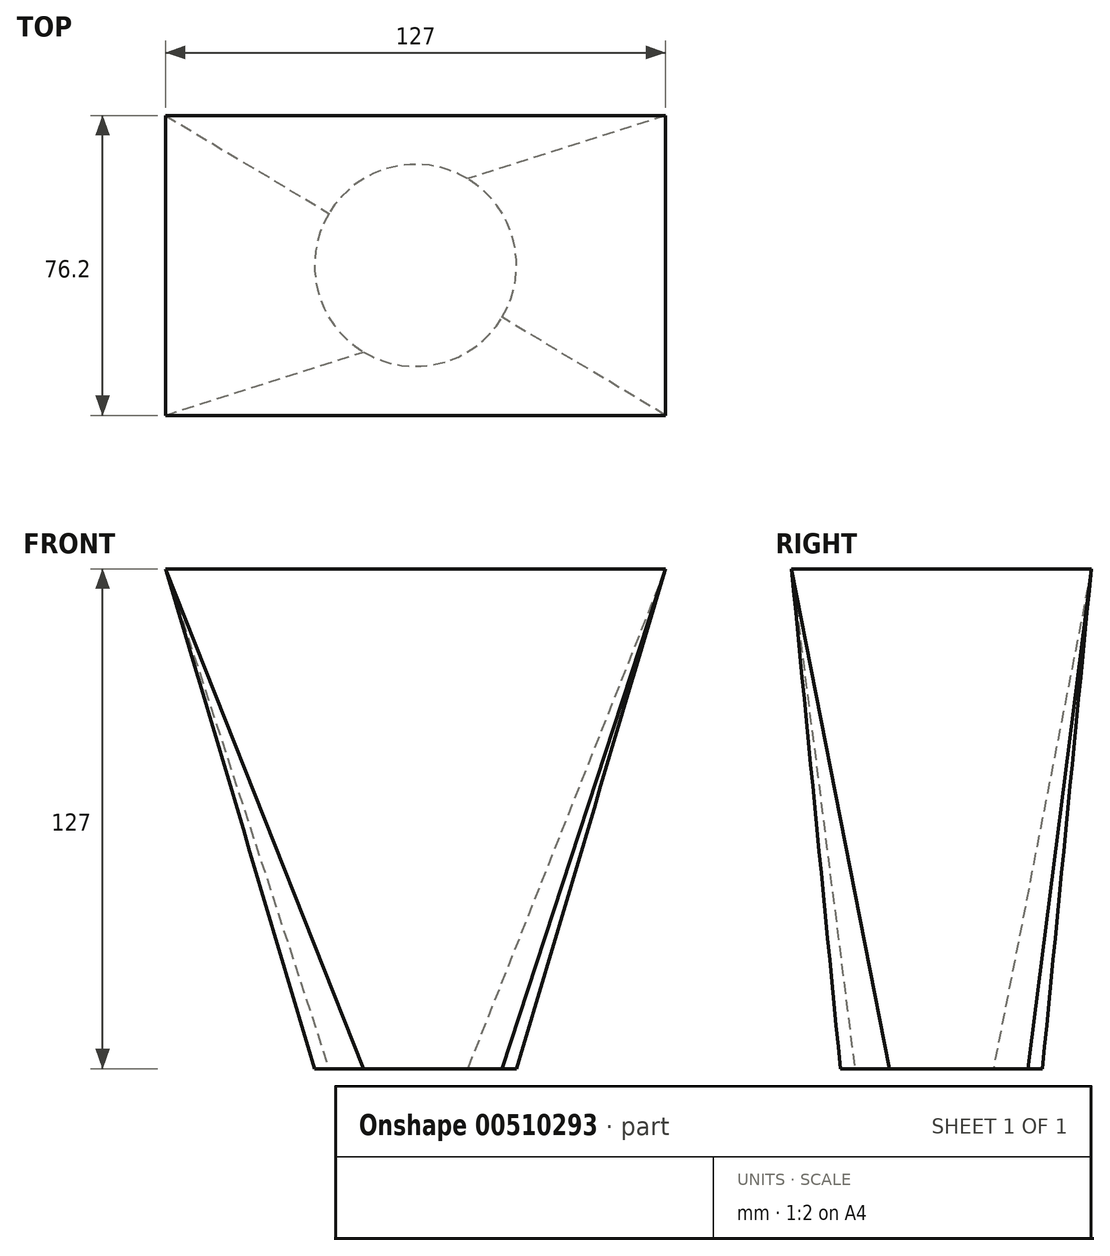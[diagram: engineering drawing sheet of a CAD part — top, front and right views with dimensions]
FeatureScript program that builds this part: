
annotation { "Feature Type Name" : "Feature", "Feature Type Description" : "" }
export const myFeature = defineFeature(function(context is Context, id is Id, definition is map)
    precondition{}
    {
        {
            var Q0;
            Q0=qCreatedBy(makeId("Top.planeOp"),FACE);
            var sketch = newSketch(context, id + "F0", { "sketchPlane" : qUnion([Q0])});
            skCircle(sketch, "E0", {"center": v(0, 0) * mm, "radius": 25.65 * mm});
            skSolve(sketch);
        }
        {
            var Q0;
            Q0=qCreatedBy(makeId("Top.planeOp"),FACE);
            cPlane(context, id + "F1", {"entities" : qUnion([Q0]), "cplaneType" : CPlaneType.OFFSET, "offset" : 127 * mm, "width" : 152.4 * mm, "height" : 152.4 * mm});
        }
        {
            var Q0;
            Q0=qCreatedBy(id+"F1.planeOp",FACE);
            var sketch = newSketch(context, id + "F2", { "sketchPlane" : qUnion([Q0])});
            skLineSegment(sketch, "E1.bottom", {"start": v(63.5, -38.1) * mm, "end": v(-63.5, -38.1) * mm});
            skLineSegment(sketch, "E1.top", {"start": v(63.5, 38.1) * mm, "end": v(-63.5, 38.1) * mm});
            skLineSegment(sketch, "E1.left", {"start": v(63.5, -38.1) * mm, "end": v(63.5, 38.1) * mm});
            skLineSegment(sketch, "E1.right", {"start": v(-63.5, -38.1) * mm, "end": v(-63.5, 38.1) * mm});
            skPoint(sketch, "E1.middle", {"position": v(0, 0) * mm});
            skSolve(sketch);
        }
        {
            var Q0;
            Q0=makeQuery(id+"F2.imprint","IMPRINT",FACE,{"disambiguationData":[TD([[makeQuery(id+"F2.imprint","IMPRINT",EDGE,{"derivedFrom":sQuery(id+"F2.wireOp",EDGE,"E1.bottom")}),-1.0]])]});
            var Q1;
            Q1=makeQuery(id+"F0.imprint","IMPRINT",FACE,{"disambiguationData":[TD([[makeQuery(id+"F0.imprint","IMPRINT",EDGE,{"derivedFrom":sQuery(id+"F0.wireOp",EDGE,"E0")}),1.0]])]});
            loft(context, id + "F3", {"sheetProfilesArray" : [{ "sheetProfileEntities" : qUnion([Q0]) }, { "sheetProfileEntities" : qUnion([Q1]) }]});
        }
    });
